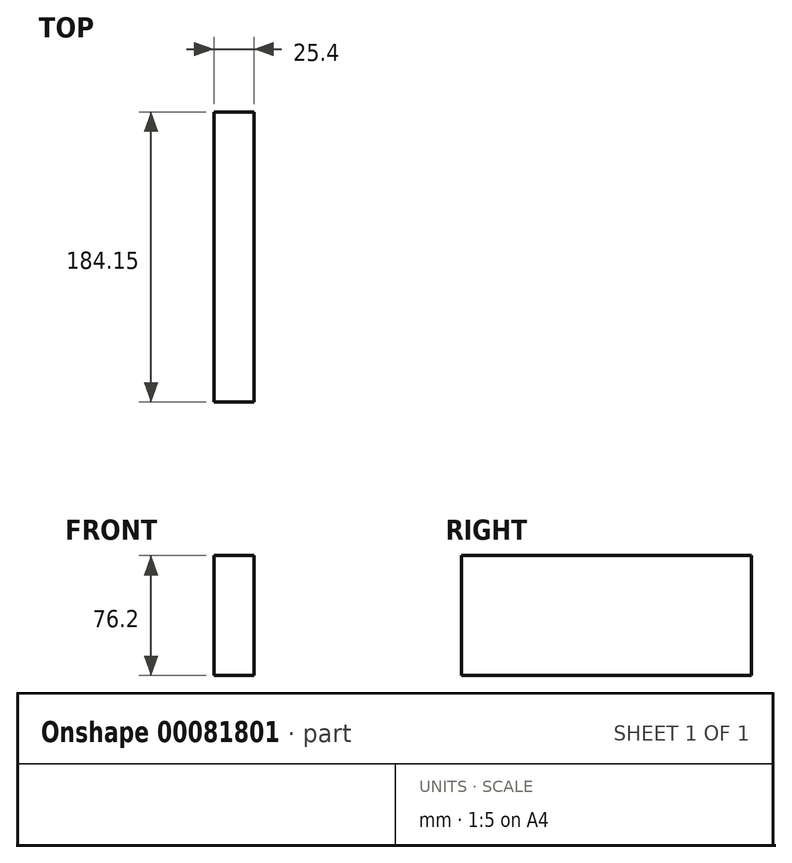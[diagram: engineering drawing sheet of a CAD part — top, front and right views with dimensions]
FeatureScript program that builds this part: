
annotation { "Feature Type Name" : "Feature", "Feature Type Description" : "" }
export const myFeature = defineFeature(function(context is Context, id is Id, definition is map)
    precondition{}
    {
        {
            var Q0;
            Q0=qCreatedBy(makeId("Top.planeOp"),FACE);
            var sketch = newSketch(context, id + "F0", { "sketchPlane" : qUnion([Q0])});
            skLineSegment(sketch, "E0.bottom", {"start": v(-68.57, 99.5) * mm, "end": v(-43.17, 99.5) * mm});
            skLineSegment(sketch, "E0.top", {"start": v(-68.57, -84.64) * mm, "end": v(-43.17, -84.64) * mm});
            skLineSegment(sketch, "E0.left", {"start": v(-68.57, 99.5) * mm, "end": v(-68.57, -84.64) * mm});
            skLineSegment(sketch, "E0.right", {"start": v(-43.17, 99.5) * mm, "end": v(-43.17, -84.64) * mm});
            skSolve(sketch);
        }
        {
            var Q0;
            Q0=makeQuery(id+"F0.imprint","IMPRINT",FACE,{"disambiguationData":[TD([[makeQuery(id+"F0.imprint","IMPRINT",EDGE,{"derivedFrom":sQuery(id+"F0.wireOp",EDGE,"E0.bottom")}),-1.0]])]});
            extrude(context, id + "F1", {"entities" : qUnion([Q0]), "depth" : 76.2 * mm});
        }
    });
